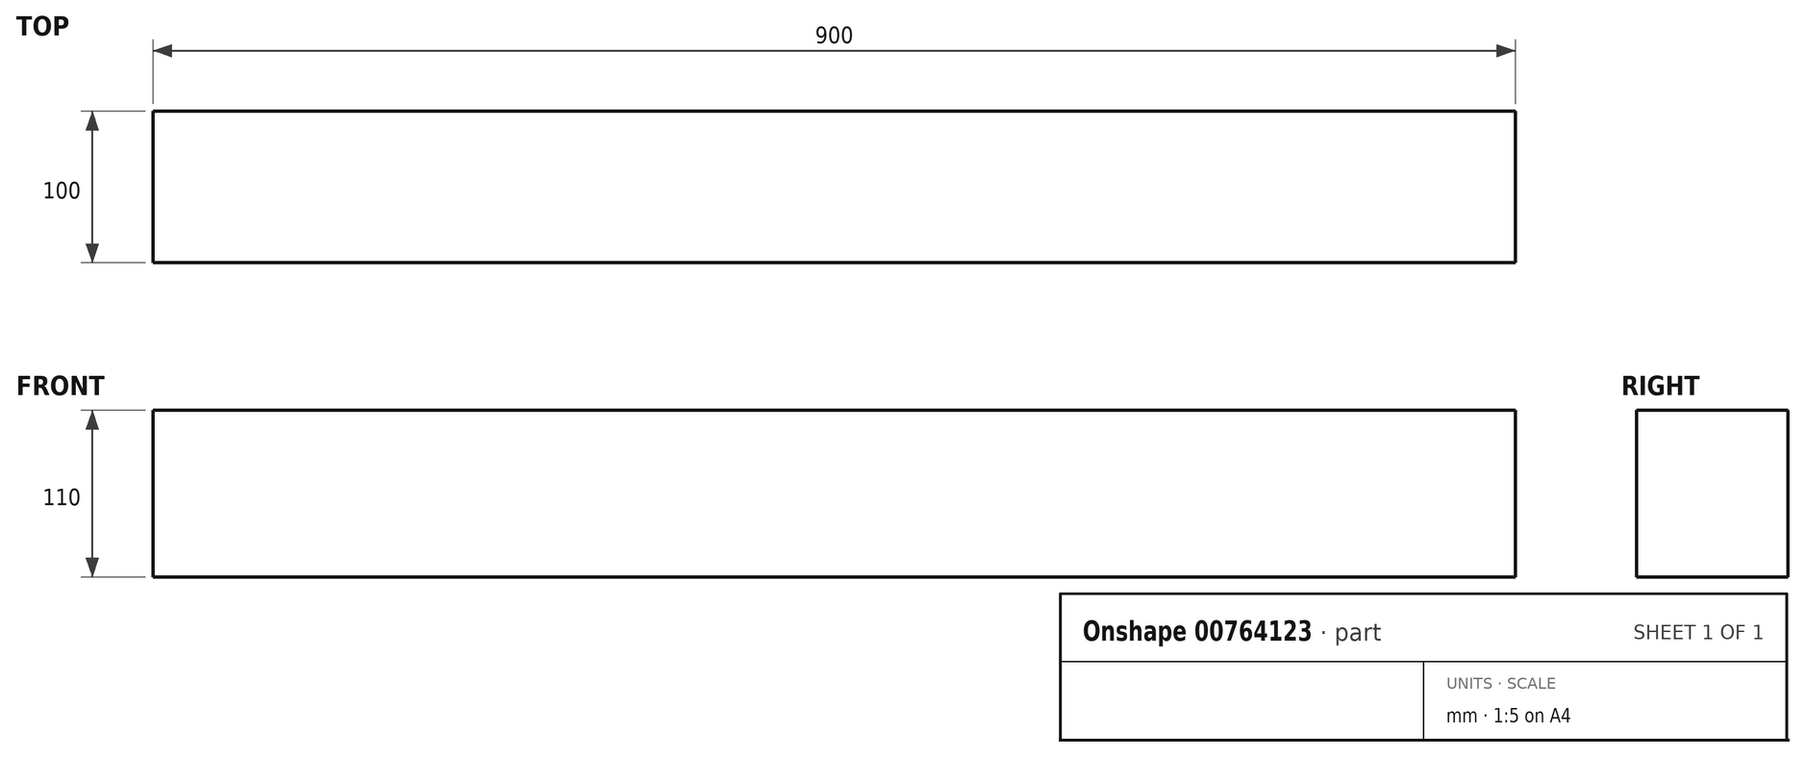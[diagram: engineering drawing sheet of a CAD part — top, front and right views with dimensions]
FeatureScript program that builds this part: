
annotation { "Feature Type Name" : "Feature", "Feature Type Description" : "" }
export const myFeature = defineFeature(function(context is Context, id is Id, definition is map)
    precondition{}
    {
        {
            var Q0;
            Q0=qCreatedBy(makeId("Front.planeOp"),FACE);
            var sketch = newSketch(context, id + "F0", { "sketchPlane" : qUnion([Q0])});
            skLineSegment(sketch, "E0.bottom", {"start": v(0, 0) * mm, "end": v(900, 0) * mm});
            skLineSegment(sketch, "E0.top", {"start": v(0, 110) * mm, "end": v(900, 110) * mm});
            skLineSegment(sketch, "E0.left", {"start": v(0, 0) * mm, "end": v(0, 110) * mm});
            skLineSegment(sketch, "E0.right", {"start": v(900, 0) * mm, "end": v(900, 110) * mm});
            skSolve(sketch);
        }
        {
            var Q0;
            Q0 = qSketchRegion(id + "F0", true);
            extrude(context, id + "F1", {"entities" : qUnion([Q0]), "oppositeDirection" : true, "depth" : 100 * mm, "offsetDistance" : 25 * mm});
        }
    });
